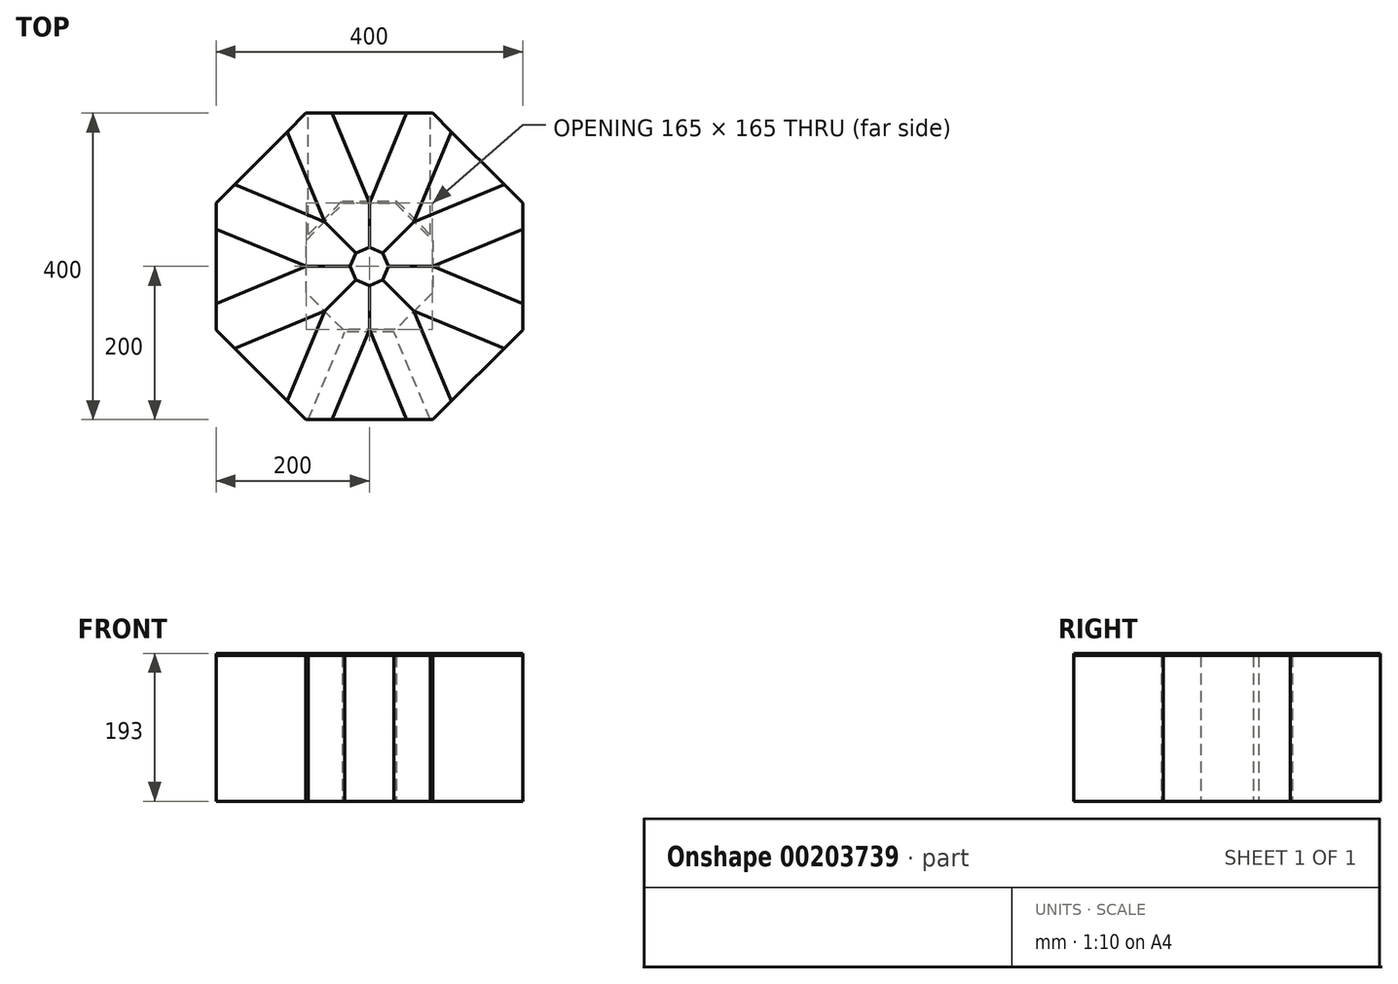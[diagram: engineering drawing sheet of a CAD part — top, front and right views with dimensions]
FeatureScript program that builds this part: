
annotation { "Feature Type Name" : "Feature", "Feature Type Description" : "" }
export const myFeature = defineFeature(function(context is Context, id is Id, definition is map)
    precondition{}
    {
        {
            var Q0;
            Q0=qCreatedBy(makeId("Top.planeOp"),FACE);
            var sketch = newSketch(context, id + "F0", { "sketchPlane" : qUnion([Q0])});
            skCircle(sketch, "E0.cCircle", {"center": v(0, 0) * mm, "radius": 200 * mm, "construction": true});
            skLineSegment(sketch, "E0.0", {"start": v(200, 82.84) * mm, "end": v(200, -82.84) * mm});
            skLineSegment(sketch, "E0.1", {"start": v(200, -82.84) * mm, "end": v(82.84, -200) * mm});
            skLineSegment(sketch, "E0.2", {"start": v(82.84, -200) * mm, "end": v(-82.84, -200) * mm});
            skLineSegment(sketch, "E0.3", {"start": v(-82.84, -200) * mm, "end": v(-200, -82.84) * mm});
            skLineSegment(sketch, "E0.4", {"start": v(-200, -82.84) * mm, "end": v(-200, 82.84) * mm});
            skLineSegment(sketch, "E0.5", {"start": v(-200, 82.84) * mm, "end": v(-82.84, 200) * mm});
            skLineSegment(sketch, "E0.6", {"start": v(-82.84, 200) * mm, "end": v(82.84, 200) * mm});
            skLineSegment(sketch, "E0.7", {"start": v(82.84, 200) * mm, "end": v(200, 82.84) * mm});
            skPoint(sketch, "E0.0.midPoint", {"position": v(200, 0) * mm});
            skCircle(sketch, "E1.cCircle", {"center": v(0, 0) * mm, "radius": 82.5 * mm, "construction": true});
            skLineSegment(sketch, "E1.0", {"start": v(82.5, 34.17) * mm, "end": v(82.5, -34.17) * mm});
            skLineSegment(sketch, "E1.1", {"start": v(82.5, -34.17) * mm, "end": v(34.17, -82.5) * mm});
            skLineSegment(sketch, "E1.2", {"start": v(34.17, -82.5) * mm, "end": v(-34.17, -82.5) * mm});
            skLineSegment(sketch, "E1.3", {"start": v(-34.17, -82.5) * mm, "end": v(-82.5, -34.17) * mm});
            skLineSegment(sketch, "E1.4", {"start": v(-82.5, -34.17) * mm, "end": v(-82.5, 34.17) * mm});
            skLineSegment(sketch, "E1.5", {"start": v(-82.5, 34.17) * mm, "end": v(-34.17, 82.5) * mm});
            skLineSegment(sketch, "E1.6", {"start": v(-34.17, 82.5) * mm, "end": v(34.17, 82.5) * mm});
            skLineSegment(sketch, "E1.7", {"start": v(34.17, 82.5) * mm, "end": v(82.5, 34.17) * mm});
            skPoint(sketch, "E1.0.midPoint", {"position": v(82.5, 0) * mm});
            skLineSegment(sketch, "E2.bottom", {"start": v(-82.84, 200) * mm, "end": v(82.84, 200) * mm, "construction": true});
            skLineSegment(sketch, "E2.top", {"start": v(-82.84, 82.5) * mm, "end": v(82.84, 82.5) * mm, "construction": true});
            skLineSegment(sketch, "E2.left", {"start": v(-82.84, 200) * mm, "end": v(-82.84, 82.5) * mm, "construction": true});
            skLineSegment(sketch, "E2.right", {"start": v(82.84, 200) * mm, "end": v(82.84, 82.5) * mm, "construction": true});
            skLineSegment(sketch, "E3", {"start": v(82.84, 82.5) * mm, "end": v(200, 82.84) * mm, "construction": true});
            skLineSegment(sketch, "E4", {"start": v(-34.17, -82.5) * mm, "end": v(-82.84, -200) * mm, "construction": true});
            skLineSegment(sketch, "E5", {"start": v(34.17, -82.5) * mm, "end": v(82.84, -200) * mm, "construction": true});
            skSolve(sketch);
        }
        {
            var Q0;
            Q0=makeQuery(id+"F0.imprint","IMPRINT",FACE,{"disambiguationData":[TD([[makeQuery(id+"F0.imprint","IMPRINT",EDGE,{"derivedFrom":sQuery(id+"F0.wireOp",EDGE,"E0.0")}),-1.0]])]});
            extrude(context, id + "F1", {"entities" : qUnion([Q0]), "depth" : 190 * mm});
        }
        {
            var Q0;
            Q0=makeQuery(id+"F1.opExtrude","CAP_FACE",FACE,{"disambiguationData":[OSD([sQuery(id+"F0.wireOp",EDGE,"E0.0"),sQuery(id+"F0.wireOp",EDGE,"E0.1"),sQuery(id+"F0.wireOp",EDGE,"E0.2"),sQuery(id+"F0.wireOp",EDGE,"E0.3"),sQuery(id+"F0.wireOp",EDGE,"E0.4"),sQuery(id+"F0.wireOp",EDGE,"E0.5"),sQuery(id+"F0.wireOp",EDGE,"E0.6"),sQuery(id+"F0.wireOp",EDGE,"E0.7"),sQuery(id+"F0.wireOp",EDGE,"E1.0"),sQuery(id+"F0.wireOp",EDGE,"E1.1"),sQuery(id+"F0.wireOp",EDGE,"E1.2"),sQuery(id+"F0.wireOp",EDGE,"E1.3"),sQuery(id+"F0.wireOp",EDGE,"E1.4"),sQuery(id+"F0.wireOp",EDGE,"E1.5"),sQuery(id+"F0.wireOp",EDGE,"E1.6"),sQuery(id+"F0.wireOp",EDGE,"E1.7")])],"isStart":false});
            var sketch = newSketch(context, id + "F2", { "sketchPlane" : qUnion([Q0])});
            skLineSegment(sketch, "E6", {"start": v(-34.17, -82.5) * mm, "end": v(-82.84, -200) * mm, "construction": true});
            skLineSegment(sketch, "E7", {"start": v(0, -82.5) * mm, "end": v(-48.67, -200) * mm});
            skLineSegment(sketch, "E8", {"start": v(0, -82.5) * mm, "end": v(0, -200) * mm, "construction": true});
            skLineSegment(sketch, "E9.MirrorCS", {"start": v(0, -82.5) * mm, "end": v(48.67, -200) * mm});
            skLineSegment(sketch, "E10", {"start": v(-48.67, -200) * mm, "end": v(48.67, -200) * mm});
            skLineSegment(sketch, "E11.1.0", {"start": v(58.34, -58.34) * mm, "end": v(107, -175.84) * mm});
            skLineSegment(sketch, "E11.1.1", {"start": v(58.34, -58.34) * mm, "end": v(175.84, -107) * mm});
            skLineSegment(sketch, "E11.1.2", {"start": v(107, -175.84) * mm, "end": v(175.84, -107) * mm});
            skLineSegment(sketch, "E11.2.0", {"start": v(82.5, 0) * mm, "end": v(200, -48.67) * mm});
            skLineSegment(sketch, "E11.2.1", {"start": v(82.5, 0) * mm, "end": v(200, 48.67) * mm});
            skLineSegment(sketch, "E11.2.2", {"start": v(200, -48.67) * mm, "end": v(200, 48.67) * mm});
            skLineSegment(sketch, "E11.3.0", {"start": v(58.34, 58.34) * mm, "end": v(175.84, 107) * mm});
            skLineSegment(sketch, "E11.3.1", {"start": v(58.34, 58.34) * mm, "end": v(107, 175.84) * mm});
            skLineSegment(sketch, "E11.3.2", {"start": v(175.84, 107) * mm, "end": v(107, 175.84) * mm});
            skLineSegment(sketch, "E11.4.0", {"start": v(0, 82.5) * mm, "end": v(48.67, 200) * mm});
            skLineSegment(sketch, "E11.4.1", {"start": v(0, 82.5) * mm, "end": v(-48.67, 200) * mm});
            skLineSegment(sketch, "E11.4.2", {"start": v(48.67, 200) * mm, "end": v(-48.67, 200) * mm});
            skLineSegment(sketch, "E11.5.0", {"start": v(-58.34, 58.34) * mm, "end": v(-107, 175.84) * mm});
            skLineSegment(sketch, "E11.5.1", {"start": v(-58.34, 58.34) * mm, "end": v(-175.84, 107) * mm});
            skLineSegment(sketch, "E11.5.2", {"start": v(-107, 175.84) * mm, "end": v(-175.84, 107) * mm});
            skLineSegment(sketch, "E11.6.0", {"start": v(-82.5, 0) * mm, "end": v(-200, 48.67) * mm});
            skLineSegment(sketch, "E11.6.1", {"start": v(-82.5, 0) * mm, "end": v(-200, -48.67) * mm});
            skLineSegment(sketch, "E11.6.2", {"start": v(-200, 48.67) * mm, "end": v(-200, -48.67) * mm});
            skLineSegment(sketch, "E11.7.0", {"start": v(-58.34, -58.34) * mm, "end": v(-175.84, -107) * mm});
            skLineSegment(sketch, "E11.7.1", {"start": v(-58.34, -58.34) * mm, "end": v(-107, -175.84) * mm});
            skLineSegment(sketch, "E11.7.2", {"start": v(-175.84, -107) * mm, "end": v(-107, -175.84) * mm});
            skPoint(sketch, "E11.center", {"position": v(0, 0) * mm});
            skSolve(sketch);
        }
        {
            var Q0;
            Q0 = qSketchRegion(id + "F2", true);
            extrude(context, id + "F3", {"entities" : qUnion([Q0]), "depth" : 3 * mm});
        }
        {
            var Q0;
            Q0=makeQuery(id+"F1.opExtrude","CAP_FACE",FACE,{"disambiguationData":[OSD([sQuery(id+"F0.wireOp",EDGE,"E0.0"),sQuery(id+"F0.wireOp",EDGE,"E0.1"),sQuery(id+"F0.wireOp",EDGE,"E0.2"),sQuery(id+"F0.wireOp",EDGE,"E0.3"),sQuery(id+"F0.wireOp",EDGE,"E0.4"),sQuery(id+"F0.wireOp",EDGE,"E0.5"),sQuery(id+"F0.wireOp",EDGE,"E0.6"),sQuery(id+"F0.wireOp",EDGE,"E0.7"),sQuery(id+"F0.wireOp",EDGE,"E1.0"),sQuery(id+"F0.wireOp",EDGE,"E1.1"),sQuery(id+"F0.wireOp",EDGE,"E1.2"),sQuery(id+"F0.wireOp",EDGE,"E1.3"),sQuery(id+"F0.wireOp",EDGE,"E1.4"),sQuery(id+"F0.wireOp",EDGE,"E1.5"),sQuery(id+"F0.wireOp",EDGE,"E1.6"),sQuery(id+"F0.wireOp",EDGE,"E1.7")])],"isStart":false});
            var sketch = newSketch(context, id + "F4", { "sketchPlane" : qUnion([Q0])});
            skLineSegment(sketch, "E12.0", {"start": v(0, 82.5) * mm, "end": v(48.67, 200) * mm});
            skLineSegment(sketch, "E13.0", {"start": v(58.34, 58.34) * mm, "end": v(107, 175.84) * mm});
            skPoint(sketch, "E14.0", {"position": v(82.84, 200) * mm});
            skLineSegment(sketch, "E15", {"start": v(48.67, 200) * mm, "end": v(82.84, 200) * mm});
            skLineSegment(sketch, "E16", {"start": v(82.84, 200) * mm, "end": v(0, 0) * mm, "construction": true});
            skLineSegment(sketch, "E17", {"start": v(0, 82.5) * mm, "end": v(0, 24.9) * mm});
            skLineSegment(sketch, "E18.MirrorCS", {"start": v(58.34, 58.34) * mm, "end": v(17.6, 17.6) * mm});
            skLineSegment(sketch, "E19", {"start": v(82.84, 200) * mm, "end": v(107, 175.84) * mm});
            skLineSegment(sketch, "E20", {"start": v(0, 24.9) * mm, "end": v(17.6, 17.6) * mm});
            skSolve(sketch);
        }
        {
            var Q0;
            {var subQ3=sQuery(id+"F4.wireOp",EDGE,"E17");Q0=makeQuery(id+"F4.imprint","IMPRINT",FACE,{"disambiguationData":[TD([[makeQuery(id+"F4.imprint","IMPRINT",EDGE,{"derivedFrom":subQ3}),1.0]])]});}
            var Q1;
            {var subQ1=sQuery(id+"F4.wireOp",EDGE,"E12.0");Q1=makeQuery(id+"F4.imprint","IMPRINT",FACE,{"disambiguationData":[TD([[makeQuery(id+"F4.imprint","IMPRINT",EDGE,{"derivedFrom":subQ1}),-1.0]])]});}
            extrude(context, id + "F5", {"entities" : qUnion([Q0, Q1]), "depth" : 3 * mm});
        }
        {
            var Q0;
            Q0=qCreatedBy(makeId("Front.planeOp"),FACE);
            var sketch = newSketch(context, id + "F6", { "sketchPlane" : qUnion([Q0])});
            skLineSegment(sketch, "E21", {"start": v(0, 0) * mm, "end": v(0, 199.22) * mm, "construction": true});
            skSolve(sketch);
        }
        {
            var Q0;
            Q0=makeQuery(id+"F5.opExtrude","SWEPT_BODY",BODY,{"disambiguationData":[OSD([sQuery(id+"F4.wireOp",EDGE,"E12.0"),sQuery(id+"F4.wireOp",EDGE,"E13.0"),sQuery(id+"F4.wireOp",EDGE,"E15"),sQuery(id+"F4.wireOp",EDGE,"E17"),sQuery(id+"F4.wireOp",EDGE,"E18.MirrorCS"),sQuery(id+"F4.wireOp",EDGE,"E19"),sQuery(id+"F4.wireOp",EDGE,"E20")])]});
            var Q1;
            Q1=sQuery(id+"F6.wireOp",EDGE,"E21");
            circularPattern(context, id + "F7", {"entities" : qUnion([Q0]), "axis" : qUnion([Q1]), "angle" : 360 * degree, "instanceCount" : 8, "equalSpace" : true});
        }
        {
            var Q0;
            Q0=makeQuery(id+"F1.opExtrude","CAP_FACE",FACE,{"disambiguationData":[OSD([sQuery(id+"F0.wireOp",EDGE,"E0.0"),sQuery(id+"F0.wireOp",EDGE,"E0.1"),sQuery(id+"F0.wireOp",EDGE,"E0.2"),sQuery(id+"F0.wireOp",EDGE,"E0.3"),sQuery(id+"F0.wireOp",EDGE,"E0.4"),sQuery(id+"F0.wireOp",EDGE,"E0.5"),sQuery(id+"F0.wireOp",EDGE,"E0.6"),sQuery(id+"F0.wireOp",EDGE,"E0.7"),sQuery(id+"F0.wireOp",EDGE,"E1.0"),sQuery(id+"F0.wireOp",EDGE,"E1.1"),sQuery(id+"F0.wireOp",EDGE,"E1.2"),sQuery(id+"F0.wireOp",EDGE,"E1.3"),sQuery(id+"F0.wireOp",EDGE,"E1.4"),sQuery(id+"F0.wireOp",EDGE,"E1.5"),sQuery(id+"F0.wireOp",EDGE,"E1.6"),sQuery(id+"F0.wireOp",EDGE,"E1.7")])],"isStart":true});
            var sketch = newSketch(context, id + "F8", { "sketchPlane" : qUnion([Q0])});
            skLineSegment(sketch, "E22", {"start": v(-82.84, 200) * mm, "end": v(-34.17, 82.5) * mm, "construction": true});
            skLineSegment(sketch, "E23", {"start": v(82.84, 200) * mm, "end": v(34.17, 82.5) * mm, "construction": true});
            skLineSegment(sketch, "E24.0", {"start": v(80.07, 201.15) * mm, "end": v(32.17, 85.5) * mm});
            skLineSegment(sketch, "E24.1", {"start": v(32.17, 85.5) * mm, "end": v(-32.17, 85.5) * mm});
            skLineSegment(sketch, "E24.2", {"start": v(-80.07, 201.15) * mm, "end": v(-32.17, 85.5) * mm});
            skLineSegment(sketch, "E25", {"start": v(-80.07, 201.15) * mm, "end": v(80.07, 201.15) * mm});
            skSolve(sketch);
        }
        {
            var Q0;
            {var subQ0=sQuery(id+"F8.wireOp",EDGE,"E24.1");Q0=makeQuery(id+"F8.imprint","IMPRINT",FACE,{"disambiguationData":[TD([[makeQuery(id+"F8.imprint","IMPRINT",EDGE,{"derivedFrom":subQ0}),-1.0]])]});}
            var Q1;
            Q1=makeQuery(id+"F1.opExtrude","CAP_FACE",FACE,{"disambiguationData":[OSD([sQuery(id+"F0.wireOp",EDGE,"E0.0"),sQuery(id+"F0.wireOp",EDGE,"E0.1"),sQuery(id+"F0.wireOp",EDGE,"E0.2"),sQuery(id+"F0.wireOp",EDGE,"E0.3"),sQuery(id+"F0.wireOp",EDGE,"E0.4"),sQuery(id+"F0.wireOp",EDGE,"E0.5"),sQuery(id+"F0.wireOp",EDGE,"E0.6"),sQuery(id+"F0.wireOp",EDGE,"E0.7"),sQuery(id+"F0.wireOp",EDGE,"E1.0"),sQuery(id+"F0.wireOp",EDGE,"E1.1"),sQuery(id+"F0.wireOp",EDGE,"E1.2"),sQuery(id+"F0.wireOp",EDGE,"E1.3"),sQuery(id+"F0.wireOp",EDGE,"E1.4"),sQuery(id+"F0.wireOp",EDGE,"E1.5"),sQuery(id+"F0.wireOp",EDGE,"E1.6"),sQuery(id+"F0.wireOp",EDGE,"E1.7")])],"isStart":false});
            extrude(context, id + "F9", {"entities" : qUnion([Q0]), "operationType" : NewBodyOperationType.REMOVE, "endBound" : BoundingType.UP_TO_SURFACE, "oppositeDirection" : true, "endBoundEntityFace" : qUnion([Q1]), "depth" : 25 * mm});
        }
        {
            var Q0;
            Q0=makeQuery(id+"F1.opExtrude","CAP_FACE",FACE,{"disambiguationData":[OSD([sQuery(id+"F0.wireOp",EDGE,"E0.0"),sQuery(id+"F0.wireOp",EDGE,"E0.1"),sQuery(id+"F0.wireOp",EDGE,"E0.2"),sQuery(id+"F0.wireOp",EDGE,"E0.3"),sQuery(id+"F0.wireOp",EDGE,"E0.4"),sQuery(id+"F0.wireOp",EDGE,"E0.5"),sQuery(id+"F0.wireOp",EDGE,"E0.6"),sQuery(id+"F0.wireOp",EDGE,"E0.7"),sQuery(id+"F0.wireOp",EDGE,"E1.0"),sQuery(id+"F0.wireOp",EDGE,"E1.1"),sQuery(id+"F0.wireOp",EDGE,"E1.2"),sQuery(id+"F0.wireOp",EDGE,"E1.3"),sQuery(id+"F0.wireOp",EDGE,"E1.4"),sQuery(id+"F0.wireOp",EDGE,"E1.5"),sQuery(id+"F0.wireOp",EDGE,"E1.6"),sQuery(id+"F0.wireOp",EDGE,"E1.7")])],"isStart":true});
            var sketch = newSketch(context, id + "F10", { "sketchPlane" : qUnion([Q0])});
            skLineSegment(sketch, "E26", {"start": v(-82.5, -34.17) * mm, "end": v(-82.84, -200) * mm, "construction": true});
            skLineSegment(sketch, "E27", {"start": v(82.5, -34.17) * mm, "end": v(82.84, -200) * mm, "construction": true});
            skLineSegment(sketch, "E28.0", {"start": v(-79.51, -41.4) * mm, "end": v(-79.84, -200) * mm});
            skLineSegment(sketch, "E28.1", {"start": v(-35.42, -85.5) * mm, "end": v(35.42, -85.5) * mm});
            skLineSegment(sketch, "E28.2", {"start": v(35.42, -85.5) * mm, "end": v(79.51, -41.4) * mm});
            skLineSegment(sketch, "E28.3", {"start": v(-79.51, -41.4) * mm, "end": v(-35.42, -85.5) * mm});
            skLineSegment(sketch, "E28.4", {"start": v(79.51, -41.4) * mm, "end": v(79.84, -200) * mm});
            skLineSegment(sketch, "E29", {"start": v(-79.84, -200) * mm, "end": v(79.84, -200) * mm});
            skSolve(sketch);
        }
        {
            var Q0;
            Q0=makeQuery(id+"F10.imprint","IMPRINT",FACE,{"disambiguationData":[TD([[makeQuery(id+"F10.imprint","IMPRINT",EDGE,{"derivedFrom":sQuery(id+"F10.wireOp",EDGE,"E28.0")}),1.0]])]});
            var Q1;
            Q1=makeQuery(id+"F1.opExtrude","CAP_FACE",FACE,{"disambiguationData":[OSD([sQuery(id+"F0.wireOp",EDGE,"E0.0"),sQuery(id+"F0.wireOp",EDGE,"E0.1"),sQuery(id+"F0.wireOp",EDGE,"E0.2"),sQuery(id+"F0.wireOp",EDGE,"E0.3"),sQuery(id+"F0.wireOp",EDGE,"E0.4"),sQuery(id+"F0.wireOp",EDGE,"E0.5"),sQuery(id+"F0.wireOp",EDGE,"E0.6"),sQuery(id+"F0.wireOp",EDGE,"E0.7"),sQuery(id+"F0.wireOp",EDGE,"E1.0"),sQuery(id+"F0.wireOp",EDGE,"E1.1"),sQuery(id+"F0.wireOp",EDGE,"E1.2"),sQuery(id+"F0.wireOp",EDGE,"E1.3"),sQuery(id+"F0.wireOp",EDGE,"E1.4"),sQuery(id+"F0.wireOp",EDGE,"E1.5"),sQuery(id+"F0.wireOp",EDGE,"E1.6"),sQuery(id+"F0.wireOp",EDGE,"E1.7")])],"isStart":false});
            extrude(context, id + "F11", {"entities" : qUnion([Q0]), "operationType" : NewBodyOperationType.REMOVE, "endBound" : BoundingType.UP_TO_SURFACE, "oppositeDirection" : true, "endBoundEntityFace" : qUnion([Q1]), "depth" : 25 * mm});
        }
    });
